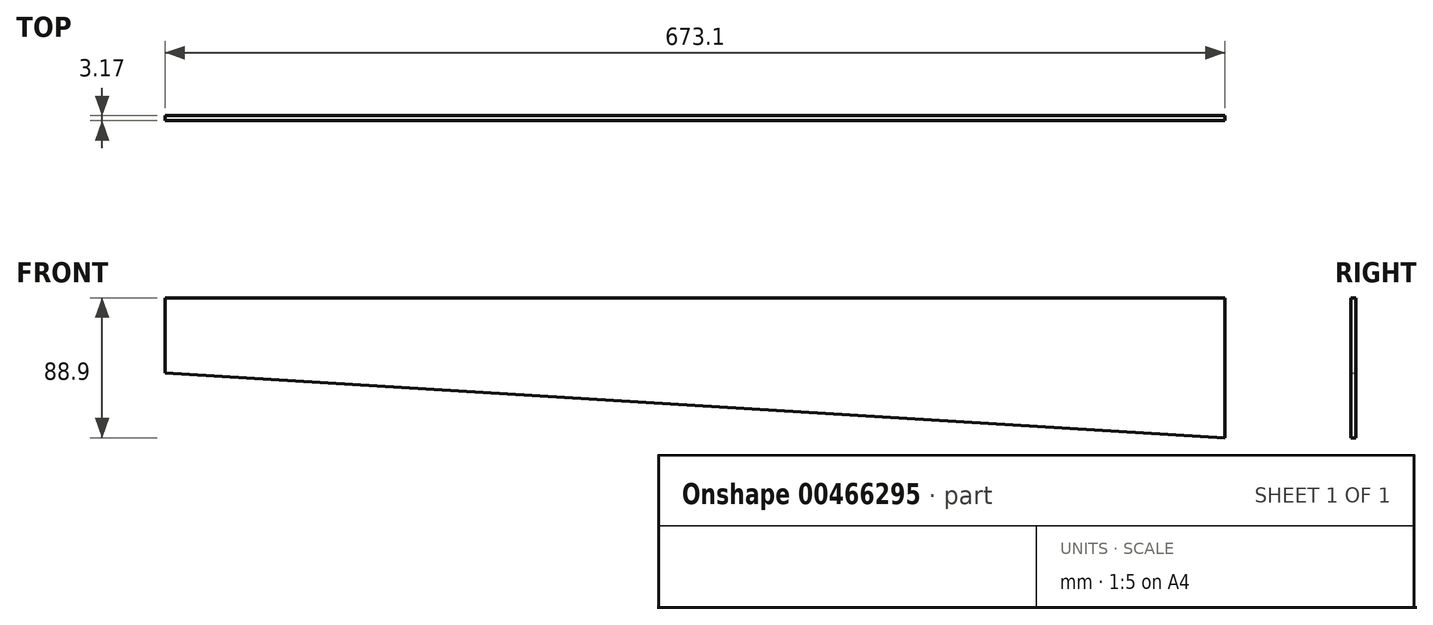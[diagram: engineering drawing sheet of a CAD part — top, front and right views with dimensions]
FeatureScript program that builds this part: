
annotation { "Feature Type Name" : "Feature", "Feature Type Description" : "" }
export const myFeature = defineFeature(function(context is Context, id is Id, definition is map)
    precondition{}
    {
        {
            var Q0;
            Q0=qCreatedBy(makeId("Front.planeOp"),FACE);
            var sketch = newSketch(context, id + "F0", { "sketchPlane" : qUnion([Q0])});
            skLineSegment(sketch, "E0", {"start": v(-202.24, -7.74) * mm, "end": v(-202.24, 39.89) * mm});
            skLineSegment(sketch, "E1", {"start": v(-202.24, 39.89) * mm, "end": v(470.86, 39.89) * mm});
            skLineSegment(sketch, "E2", {"start": v(470.86, 39.89) * mm, "end": v(470.86, -49.01) * mm});
            skLineSegment(sketch, "E3", {"start": v(470.86, -49.01) * mm, "end": v(-202.24, -7.74) * mm});
            skSolve(sketch);
        }
        {
            var Q0;
            Q0=qSketchRegion(id+"F0",true);
            extrude(context, id + "F1", {"entities" : qUnion([Q0]), "depth" : 3.17 * mm, "offsetDistance" : 25.4 * mm});
        }
    });
